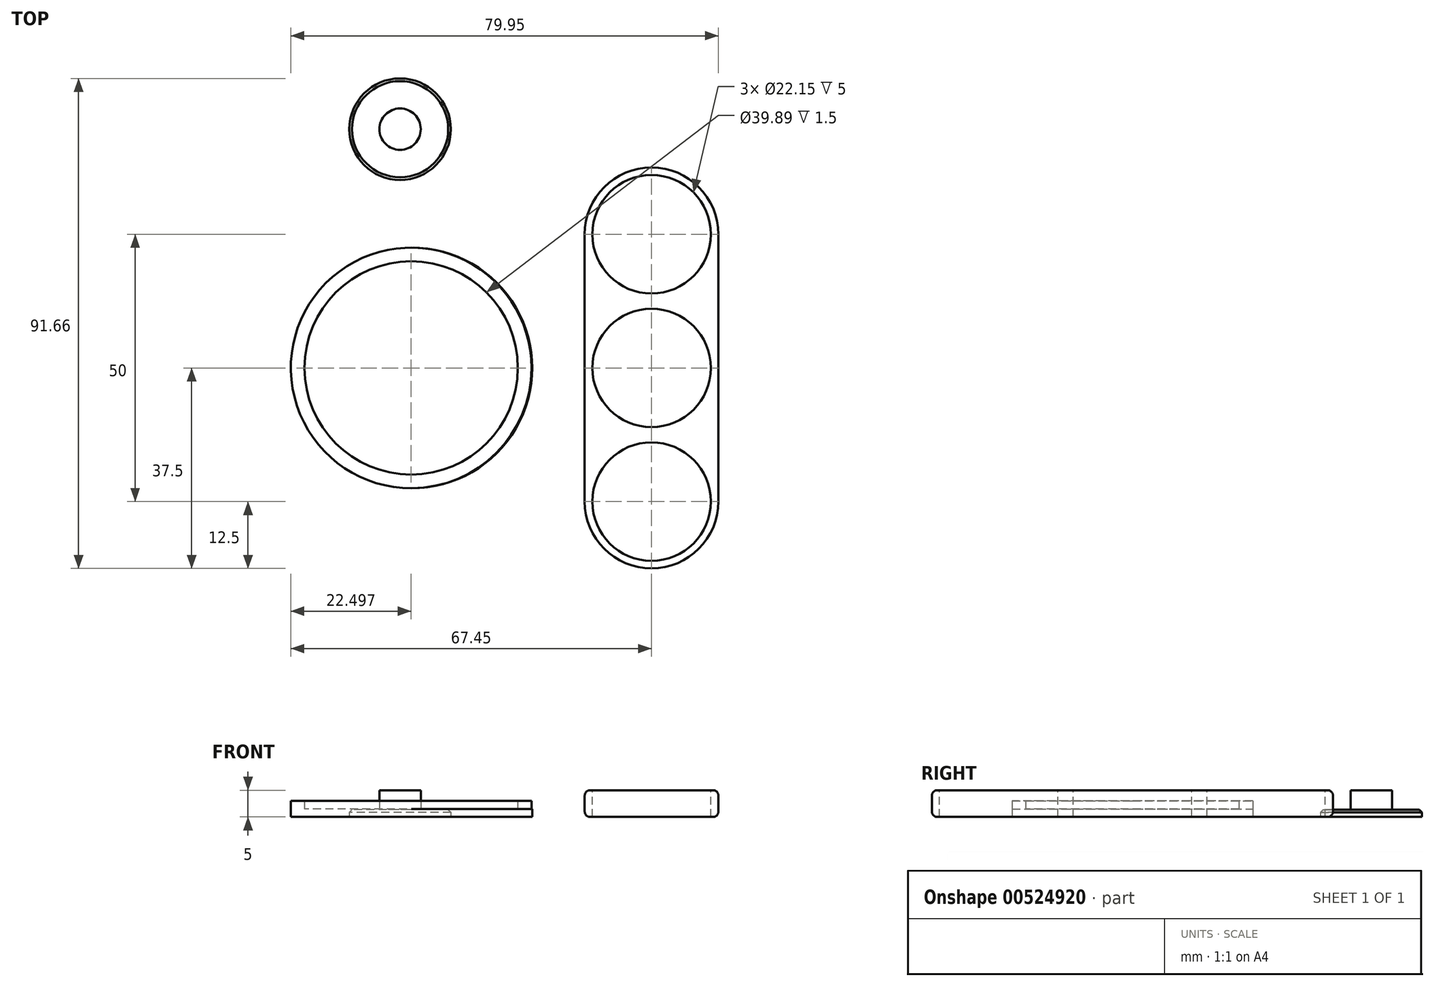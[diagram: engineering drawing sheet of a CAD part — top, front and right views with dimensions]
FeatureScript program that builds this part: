
annotation { "Feature Type Name" : "Feature", "Feature Type Description" : "" }
export const myFeature = defineFeature(function(context is Context, id is Id, definition is map)
    precondition{}
    {
        {
            var Q0;
            Q0=qCreatedBy(makeId("Top.planeOp"),FACE);
            var sketch = newSketch(context, id + "F0", { "sketchPlane" : qUnion([Q0])});
            skCircle(sketch, "E0", {"center": v(0, 0) * mm, "radius": 12.5 * mm});
            skCircle(sketch, "E1", {"center": v(0, 25) * mm, "radius": 12.5 * mm});
            skCircle(sketch, "E2", {"center": v(0, -25) * mm, "radius": 12.5 * mm});
            skLineSegment(sketch, "E3", {"start": v(-12.5, 25) * mm, "end": v(-12.5, -25) * mm});
            skLineSegment(sketch, "E4", {"start": v(12.5, 25) * mm, "end": v(12.5, -25) * mm});
            skSolve(sketch);
        }
        {
            var Q0;
            Q0 = qSketchRegion(id + "F0", true);
            extrude(context, id + "F1", {"entities" : qUnion([Q0]), "depth" : 5 * mm, "offsetDistance" : 25 * mm});
        }
        {
            var Q0;
            Q0=makeQuery(id+"F1.opExtrude","CAP_FACE",FACE,{"disambiguationData":[OSD([sQuery(id+"F0.wireOp",EDGE,"E1"),sQuery(id+"F0.wireOp",EDGE,"E2"),sQuery(id+"F0.wireOp",EDGE,"E3"),sQuery(id+"F0.wireOp",EDGE,"E4")])],"isStart":false});
            var sketch = newSketch(context, id + "F2", { "sketchPlane" : qUnion([Q0])});
            skCircle(sketch, "E5", {"center": v(0, 25) * mm, "radius": 11.07 * mm});
            skCircle(sketch, "E6", {"center": v(0, 0) * mm, "radius": 11.07 * mm});
            skCircle(sketch, "E7", {"center": v(0, -25) * mm, "radius": 11.07 * mm});
            skSolve(sketch);
        }
        {
            var Q0;
            Q0 = qSketchRegion(id + "F2", true);
            extrude(context, id + "F3", {"entities" : qUnion([Q0]), "operationType" : NewBodyOperationType.REMOVE, "oppositeDirection" : true, "depth" : 25 * mm, "offsetDistance" : 25 * mm});
        }
        {
            var Q0;
            Q0=qCreatedBy(makeId("Top.planeOp"),FACE);
            var sketch = newSketch(context, id + "F4", { "sketchPlane" : qUnion([Q0])});
            skCircle(sketch, "E8", {"center": v(-44.95, 0) * mm, "radius": 19.95 * mm});
            skCircle(sketch, "E9", {"center": v(-44.95, 0) * mm, "radius": 22.5 * mm});
            skSolve(sketch);
        }
        {
            var Q0;
            Q0 = qSketchRegion(id + "F4", true);
            var Q1;
            Q1 = qSketchRegion(id + "F6", true);
            extrude(context, id + "F5", {"entities" : qUnion([Q0, Q1]), "depth" : 3 * mm, "offsetDistance" : 25 * mm});
        }
        {
            var Q0;
            Q0=makeQuery(id+"F4.imprint","IMPRINT",FACE,{"disambiguationData":[TD([[makeQuery(id+"F4.imprint","IMPRINT",EDGE,{"derivedFrom":sQuery(id+"F4.wireOp",EDGE,"E8")}),1.0]])]});
            var sketch = newSketch(context, id + "F6", { "sketchPlane" : qUnion([Q0])});
            skCircle(sketch, "E10", {"center": v(-44.82, 0) * mm, "radius": 22.5 * mm});
            skSolve(sketch);
        }
        {
            var Q0;
            Q0 = qSketchRegion(id + "F6", true);
            extrude(context, id + "F7", {"entities" : qUnion([Q0]), "operationType" : NewBodyOperationType.ADD, "depth" : 1.5 * mm, "offsetDistance" : 25 * mm});
        }
        {
            var Q0;
            Q0=qCreatedBy(makeId("Top.planeOp"),FACE);
            var sketch = newSketch(context, id + "F8", { "sketchPlane" : qUnion([Q0])});
            skCircle(sketch, "E11", {"center": v(-47.03, 44.66) * mm, "radius": 9.5 * mm});
            skSolve(sketch);
        }
        {
            var Q0;
            Q0 = qSketchRegion(id + "F8", true);
            extrude(context, id + "F9", {"entities" : qUnion([Q0]), "depth" : 1.35 * mm, "offsetDistance" : 25 * mm});
        }
        {
            var Q0;
            Q0=makeQuery(id+"F9.opExtrude","CAP_EDGE",EDGE,{"disambiguationData":[OSD([sQuery(id+"F8.wireOp",EDGE,"E11")])],"isStart":false});
            chamfer(context, id + "F10", {"entities" : qUnion([Q0]), "width" : .5 * mm, "tangentPropagation" : true});
        }
        {
            var Q0;
            Q0=makeQuery(id+"F9.opExtrude","CAP_FACE",FACE,{"disambiguationData":[OSD([sQuery(id+"F8.wireOp",EDGE,"E11")])],"isStart":false});
            var sketch = newSketch(context, id + "F11", { "sketchPlane" : qUnion([Q0])});
            skCircle(sketch, "E12", {"center": v(-47.03, 44.66) * mm, "radius": 3.88 * mm});
            skSolve(sketch);
        }
        {
            var Q0;
            Q0 = qSketchRegion(id + "F11", true);
            extrude(context, id + "F12", {"entities" : qUnion([Q0]), "operationType" : NewBodyOperationType.ADD, "depth" : 3.65 * mm, "offsetDistance" : 25 * mm});
        }
        {
            var Q0;
            Q0=makeQuery(id+"F1.opExtrude","CAP_EDGE",EDGE,{"disambiguationData":[OSD([sQuery(id+"F0.wireOp",EDGE,"E3")])],"isStart":false});
            var Q1;
            Q1=makeQuery(id+"F1.opExtrude","CAP_EDGE",EDGE,{"disambiguationData":[OSD([sQuery(id+"F0.wireOp",EDGE,"E1")])],"isStart":false});
            var Q2;
            Q2=makeQuery(id+"F1.opExtrude","CAP_EDGE",EDGE,{"disambiguationData":[OSD([sQuery(id+"F0.wireOp",EDGE,"E2")])],"isStart":false});
            var Q3;
            Q3=makeQuery(id+"F1.opExtrude","CAP_EDGE",EDGE,{"disambiguationData":[OSD([sQuery(id+"F0.wireOp",EDGE,"E2")])],"isStart":true});
            var Q4;
            Q4=makeQuery(id+"F1.opExtrude","CAP_EDGE",EDGE,{"disambiguationData":[OSD([sQuery(id+"F0.wireOp",EDGE,"E4")])],"isStart":true});
            var Q5;
            Q5=makeQuery(id+"F1.opExtrude","CAP_EDGE",EDGE,{"disambiguationData":[OSD([sQuery(id+"F0.wireOp",EDGE,"E1")])],"isStart":true});
            var Q6;
            Q6=makeQuery(id+"F1.opExtrude","CAP_EDGE",EDGE,{"disambiguationData":[OSD([sQuery(id+"F0.wireOp",EDGE,"E3")])],"isStart":true});
            fillet(context, id + "F13", {"entities" : qUnion([Q0, Q1, Q2, Q3, Q4, Q5, Q6]), "radius" : 1 * mm, "tangentPropagation" : true, "allowEdgeOverflow" : false});
        }
    });
